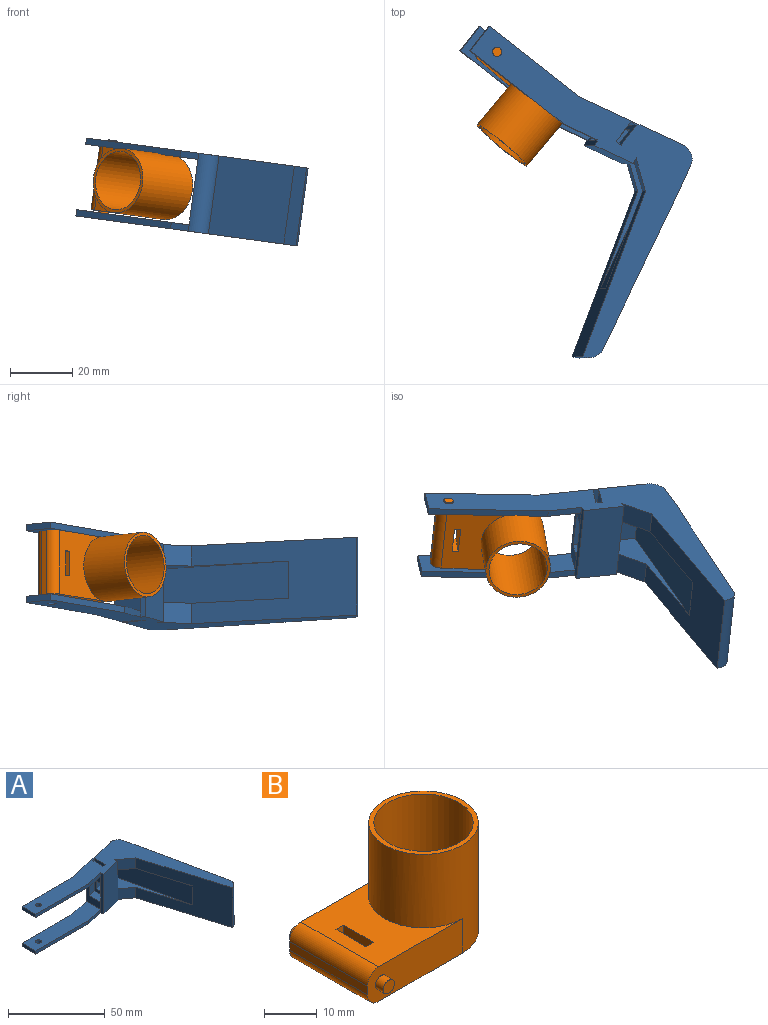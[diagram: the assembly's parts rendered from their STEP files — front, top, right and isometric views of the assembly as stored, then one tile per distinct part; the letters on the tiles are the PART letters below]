
ASSEMBLY  parts=2 mates=1
PART A: 37 faces, bbox 92.6x73.6x25.2 mm
  f0: plane 92.63x73.56mm, normal (0,0,-1), area 1326mm2, adj f2,f3,f7,f8,f12,f13,f15,f18
  f1: plane 92.63x73.56mm, normal (0,0,1), area 1326mm2, adj f2,f5,f6,f7,f8,f9,f14,f16
  f2: plane 35.82x25.17mm, normal (-0.23,0.97,0), area 643.4mm2, adj f0,f1,f4,f10,f11,f15,f16,f32
  f3: plane 11.26x2.62mm, normal (0.23,-0.97,0), area 23.1mm2, adj f0,f11,f13,f35
  f4: plane 21.17x10.41mm, normal (-1,0,0), area 121.8mm2, adj f2,f10,f11,f21,f22,f23,f35
  f5: plane 11.26x2.62mm, normal (0.23,-0.97,0), area 23.1mm2, adj f1,f10,f14,f35
  f6: plane 6.59x2mm, normal (0,1,0), area 13.2mm2, adj f1,f7,f8,f22
  f7: plane 25.17x8mm, normal (-1,0,0), area 123.9mm2, adj f0,f1,f6,f18,f19,f22,f23,f25
  f8: plane 25.17x8mm, normal (1,0,0), area 129.4mm2, adj f0,f1,f6,f18,f19,f21,f22,f23
  f9: plane 10.01x2mm, normal (-1,0,0), area 20mm2, adj f1,f10,f14,f16
  f10: plane 50x13.03mm, normal (0,0,-1), area 498.2mm2, adj f2,f4,f5,f9,f14,f16,f17
  f11: plane 50x13.03mm, normal (0,0,1), area 498.2mm2, adj f2,f3,f4,f12,f13,f15,f20
  f12: plane 10.01x2mm, normal (-1,0,0), area 20mm2, adj f0,f11,f13,f15
  f13: plane 38.74x2mm, normal (0,-1,0), area 77.5mm2, adj f0,f3,f11,f12
  f14: plane 38.74x2mm, normal (0,-1,0), area 77.5mm2, adj f1,f5,f9,f10
  f15: plane 37.02x2mm, normal (0,1,0), area 74mm2, adj f0,f2,f11,f12
  f16: plane 37.02x2mm, normal (0,1,0), area 74mm2, adj f1,f2,f9,f10
  f17: cylinder r=1.5mm len=3mm, axis (0,0,-1), area 18.8mm2, adj f1,f10
  f18: plane 6.59x2mm, normal (0,1,0), area 13.2mm2, adj f0,f7,f8,f23
  f19: plane 25.17x2mm, normal (0,-1,0), area 50.3mm2, adj f0,f1,f7,f8
  f20: cylinder r=1.5mm len=3mm, axis (0,0,-1), area 18.8mm2, adj f0,f11
  f21: plane 12x5mm, normal (0.23,-0.97,0), area 61.6mm2, adj f4,f8,f22,f23
  f22: plane 48.54x32.06mm, normal (0,0,-1), area 252.1mm2, adj f4,f6,f7,f8,f21,f24,f25,f29
  f23: plane 48.54x32.06mm, normal (0,0,1), area 252.1mm2, adj f4,f7,f8,f18,f21,f24,f25,f28
  f24: plane 48.54x12mm, normal (-0.97,-0.23,0), area 598mm2, adj f22,f23,f25,f29
  f25: plane 13.77x12mm, normal (0.23,-0.97,0), area 169.7mm2, adj f7,f22,f23,f24
  f26: plane 25.17x9.28mm, normal (0.97,0.23,0), area 239.9mm2, adj f0,f1,f27,f32
  f27: plane 54.51x25.17mm, normal (0.98,0.21,0), area 1402.4mm2, adj f0,f1,f26,f31
  f28: plane 8.95x6.59mm, normal (-0.59,-0.81,0), area 73mm2, adj f0,f23,f29,f34
  f29: plane 54.28x25.17mm, normal (-0.96,-0.29,0), area 1025.7mm2, adj f0,f1,f22,f23,f24,f28,f30,f31
  f30: plane 8.95x6.59mm, normal (-0.59,-0.81,0), area 73mm2, adj f1,f22,f29,f34
  f31: cylinder r=5mm len=25.17mm, axis (0,0,1), area 193.9mm2, adj f0,f1,f27,f29
  f32: cylinder r=5mm len=25.17mm, axis (0,0,-1), area 197.7mm2, adj f0,f1,f2,f26
  f33: plane 13.36x12mm, normal (-0.23,0.97,0), area 164.5mm2, adj f22,f23,f34,f35
  f34: plane 25.17x1.95mm, normal (0.97,0.23,0), area 50.3mm2, adj f0,f1,f28,f30,f33,f36
  f35: plane 25.17x1.95mm, normal (-0.97,-0.23,0), area 50.3mm2, adj f0,f1,f3,f4,f5,f33,f36
  f36: plane 25.17x13.36mm, normal (0.23,-0.97,0), area 345.1mm2, adj f0,f1,f34,f35
PART B: 18 faces, bbox 35.8x25x25 mm
  f0: cylinder r=10.38mm len=25mm, axis (0,0,-1), area 1370.3mm2, adj f2,f3,f4,f5,f7
  f1: cylinder r=9.38mm len=25mm, axis (0,0,-1), area 1474.2mm2, adj f2,f3
  f2: plane 20.77x20.77mm, normal (0,0,1), area 62.1mm2, adj f0,f1
  f3: plane 32.77x20.77mm, normal (0,0,-1), area 341.6mm2, adj f0,f1,f5,f7,f12,f14,f15,f16
  f4: plane 22.39x20.77mm, normal (0,0,1), area 279.5mm2, adj f0,f5,f7,f13,f14,f15,f16,f17
  f5: plane 25.39x8mm, normal (0,-1,0), area 192.1mm2, adj f0,f3,f4,f6,f10,f12,f13
  f6: plane 20.77x2mm, normal (-1,0,0), area 41.5mm2, adj f5,f7,f12,f13
  f7: plane 25.39x8mm, normal (0,1,0), area 192.1mm2, adj f0,f3,f4,f6,f9,f12,f13
  f8: plane 3x3mm, normal (0,1,0), area 7.1mm2, adj f9
  f9: cylinder r=1.5mm len=3mm, axis (0,-1,0), area 19.9mm2, adj f7,f8
  f10: cylinder r=1.5mm len=3mm, axis (0,-1,0), area 19.9mm2, adj f5,f11
  f11: plane 3x3mm, normal (0,-1,0), area 7.1mm2, adj f10
  f12: cylinder r=3mm len=20.77mm, axis (0,-1,0), area 97.9mm2, adj f3,f5,f6,f7
  f13: cylinder r=3mm len=20.77mm, axis (0,1,0), area 97.9mm2, adj f4,f5,f6,f7
  f14: plane 8x8mm, normal (1,0,0), area 64mm2, adj f3,f4,f15,f17
  f15: plane 8x2mm, normal (0,1,0), area 16mm2, adj f3,f4,f14,f16
  f16: plane 8x8mm, normal (-1,0,0), area 64mm2, adj f3,f4,f15,f17
  f17: plane 8x2mm, normal (0,-1,0), area 16mm2, adj f3,f4,f14,f16
PLACE A rot(axis=(-0.07,0.19,-0.98),38.6deg) t=(109.42,49.77,8.93)mm
PLACE B rot(axis=(0.88,-0.27,-0.39),94.4deg) t=(111.21,46.3,9.13)mm
MATE cylindrical B.f9 <-> A.f17  axis (-0.13,0,-0.99) through (93.59,57.1,23.07)mm
